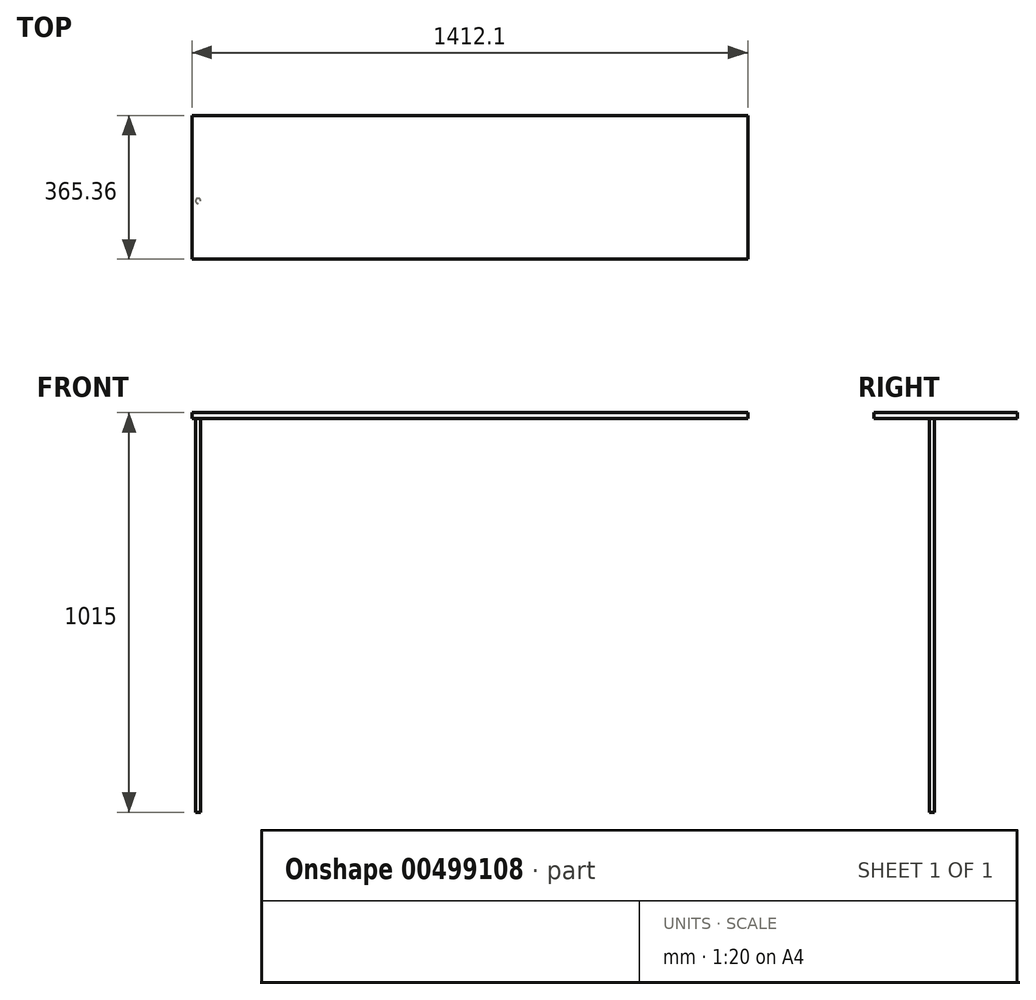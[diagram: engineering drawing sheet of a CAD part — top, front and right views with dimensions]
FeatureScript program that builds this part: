
annotation { "Feature Type Name" : "Feature", "Feature Type Description" : "" }
export const myFeature = defineFeature(function(context is Context, id is Id, definition is map)
    precondition{}
    {
        {
            var Q0;
            Q0=qCreatedBy(makeId("Top.planeOp"),FACE);
            var sketch = newSketch(context, id + "F0", { "sketchPlane" : qUnion([Q0])});
            skLineSegment(sketch, "E0.bottom", {"start": v(206.05, -115.37) * mm, "end": v(-206.05, -115.37) * mm});
            skLineSegment(sketch, "E0.top", {"start": v(206.05, 115.37) * mm, "end": v(-206.05, 115.37) * mm});
            skLineSegment(sketch, "E0.left", {"start": v(206.05, -115.37) * mm, "end": v(206.05, 115.37) * mm});
            skLineSegment(sketch, "E0.right", {"start": v(-206.05, -115.37) * mm, "end": v(-206.05, 115.37) * mm});
            skPoint(sketch, "E0.middle", {"position": v(0, 0) * mm});
            skSolve(sketch);
        }
        {
            var Q0;
            Q0 = qSketchRegion(id + "F0", true);
            extrude(context, id + "F1", {"entities" : qUnion([Q0]), "depth" : 15 * mm});
        }
        {
            var Q0;
            Q0=makeQuery(id+"F1.opExtrude","CAP_FACE",FACE,{"disambiguationData":[OSD([sQuery(id+"F0.wireOp",EDGE,"E0.bottom"),sQuery(id+"F0.wireOp",EDGE,"E0.top"),sQuery(id+"F0.wireOp",EDGE,"E0.left"),sQuery(id+"F0.wireOp",EDGE,"E0.right")])],"isStart":true});
            var sketch = newSketch(context, id + "F2", { "sketchPlane" : qUnion([Q0])});
            skCircle(sketch, "E1", {"center": v(-190.17, 101.88) * mm, "radius": 6.4 * mm});
            skSolve(sketch);
        }
        {
            var Q0;
            Q0 = qSketchRegion(id + "F2", true);
            extrude(context, id + "F3", {"entities" : qUnion([Q0]), "operationType" : NewBodyOperationType.ADD, "depth" : 1000 * mm});
        }
        {
            var Q0;
            Q0=makeQuery(id+"F1.opExtrude","SWEPT_FACE",FACE,{"disambiguationData":[OSD([sQuery(id+"F0.wireOp",EDGE,"E0.left")])]});
            extrude(context, id + "F4", {"entities" : qUnion([Q0]), "operationType" : NewBodyOperationType.ADD, "depth" : 1000 * mm});
        }
        {
            var Q0;
            {var subQ0=sQuery(id+"F0.wireOp",EDGE,"E0.bottom");Q0=makeQuery(id+"F4.boolean.opBoolean","MERGE",FACE,{"derivedFrom":[makeQuery(id+"F1.opExtrude","SWEPT_FACE",FACE,{"disambiguationData":[OSD([subQ0])]}),makeQuery(id+"F4.opExtrude","SWEPT_FACE",FACE,{"disambiguationData":[OSD([subQ0,sQuery(id+"F0.wireOp",EDGE,"E0.left")])]})]});}
            extrude(context, id + "F5", {"entities" : qUnion([Q0]), "operationType" : NewBodyOperationType.ADD, "depth" : 134.62 * mm});
        }
    });
